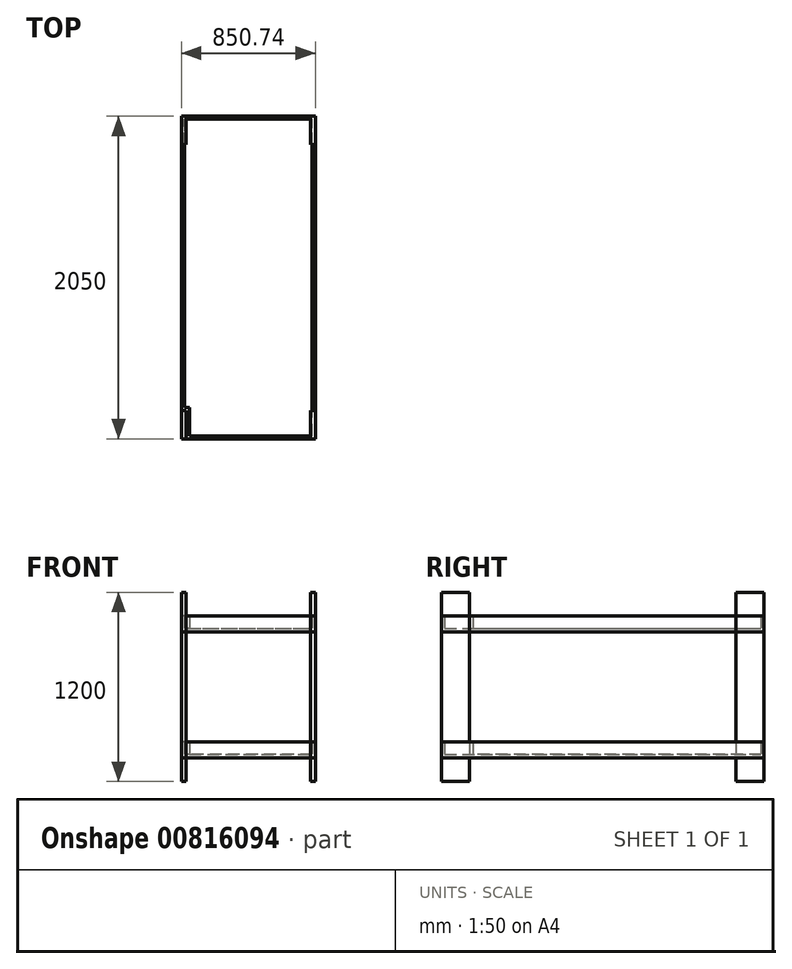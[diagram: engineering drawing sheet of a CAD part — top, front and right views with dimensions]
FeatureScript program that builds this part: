
annotation { "Feature Type Name" : "Feature", "Feature Type Description" : "" }
export const myFeature = defineFeature(function(context is Context, id is Id, definition is map)
    precondition{}
    {
        {
            var Q0;
            Q0=qCreatedBy(makeId("Top.planeOp"),FACE);
            var sketch = newSketch(context, id + "F0", { "sketchPlane" : qUnion([Q0])});
            skLineSegment(sketch, "E0.bottom", {"start": v(-156.82, -88.98) * mm, "end": v(-186.82, -88.98) * mm});
            skLineSegment(sketch, "E0.top", {"start": v(-156.82, 91.02) * mm, "end": v(-186.82, 91.02) * mm});
            skLineSegment(sketch, "E0.left", {"start": v(-156.82, -88.98) * mm, "end": v(-156.82, 91.02) * mm});
            skLineSegment(sketch, "E0.right", {"start": v(-186.82, -88.98) * mm, "end": v(-186.82, 91.02) * mm});
            skPoint(sketch, "E0.middle", {"position": v(-171.82, 1.02) * mm});
            skLineSegment(sketch, "E1.bottom", {"start": v(663.18, 1781.02) * mm, "end": v(633.18, 1781.02) * mm});
            skLineSegment(sketch, "E1.top", {"start": v(663.18, 1961.02) * mm, "end": v(633.18, 1961.02) * mm});
            skLineSegment(sketch, "E1.left", {"start": v(663.18, 1781.02) * mm, "end": v(663.18, 1961.02) * mm});
            skLineSegment(sketch, "E1.right", {"start": v(633.18, 1781.02) * mm, "end": v(633.18, 1961.02) * mm});
            skPoint(sketch, "E1.middle", {"position": v(648.18, 1871.02) * mm});
            skLineSegment(sketch, "E2.bottom", {"start": v(663.18, -88.98) * mm, "end": v(633.18, -88.98) * mm});
            skLineSegment(sketch, "E2.top", {"start": v(663.18, 91.02) * mm, "end": v(633.18, 91.02) * mm});
            skLineSegment(sketch, "E2.left", {"start": v(663.18, -88.98) * mm, "end": v(663.18, 91.02) * mm});
            skLineSegment(sketch, "E2.right", {"start": v(633.18, -88.98) * mm, "end": v(633.18, 91.02) * mm});
            skPoint(sketch, "E2.middle", {"position": v(648.18, 1.02) * mm});
            skLineSegment(sketch, "E3.bottom", {"start": v(-156.82, 1781.02) * mm, "end": v(-186.82, 1781.02) * mm});
            skLineSegment(sketch, "E3.top", {"start": v(-156.82, 1961.02) * mm, "end": v(-186.82, 1961.02) * mm});
            skLineSegment(sketch, "E3.left", {"start": v(-156.82, 1781.02) * mm, "end": v(-156.82, 1961.02) * mm});
            skLineSegment(sketch, "E3.right", {"start": v(-186.82, 1781.02) * mm, "end": v(-186.82, 1961.02) * mm});
            skPoint(sketch, "E3.middle", {"position": v(-171.82, 1871.02) * mm});
            skLineSegment(sketch, "E4", {"start": v(-186.82, -88.98) * mm, "end": v(663.18, -88.98) * mm, "construction": true});
            skLineSegment(sketch, "E5", {"start": v(-186.82, 1961.02) * mm, "end": v(663.18, 1961.02) * mm, "construction": true});
            skLineSegment(sketch, "E6", {"start": v(-186.82, 1961.02) * mm, "end": v(-186.82, -88.98) * mm, "construction": true});
            skLineSegment(sketch, "E7", {"start": v(663.18, 1961.02) * mm, "end": v(663.18, -88.98) * mm, "construction": true});
            skSolve(sketch);
        }
        {
            var Q0;
            Q0=makeQuery(id+"F0.imprint","IMPRINT",FACE,{"disambiguationData":[TD([[makeQuery(id+"F0.imprint","IMPRINT",EDGE,{"derivedFrom":sQuery(id+"F0.wireOp",EDGE,"E3.bottom")}),-1.0]])]});
            var Q1;
            Q1=makeQuery(id+"F0.imprint","IMPRINT",FACE,{"disambiguationData":[TD([[makeQuery(id+"F0.imprint","IMPRINT",EDGE,{"derivedFrom":sQuery(id+"F0.wireOp",EDGE,"E1.bottom")}),-1.0]])]});
            var Q2;
            Q2=makeQuery(id+"F0.imprint","IMPRINT",FACE,{"disambiguationData":[TD([[makeQuery(id+"F0.imprint","IMPRINT",EDGE,{"derivedFrom":sQuery(id+"F0.wireOp",EDGE,"E0.bottom")}),-1.0]])]});
            var Q3;
            Q3=makeQuery(id+"F0.imprint","IMPRINT",FACE,{"disambiguationData":[TD([[makeQuery(id+"F0.imprint","IMPRINT",EDGE,{"derivedFrom":sQuery(id+"F0.wireOp",EDGE,"E2.bottom")}),-1.0]])]});
            extrude(context, id + "F1", {"entities" : qUnion([Q0, Q1, Q2, Q3]), "depth" : 150 * mm, "offsetDistance" : 25 * mm});
        }
        {
            var Q0;
            Q0=makeQuery(id+"F1.opExtrude","CAP_FACE",FACE,{"disambiguationData":[OSD([sQuery(id+"F0.wireOp",EDGE,"E0.bottom"),sQuery(id+"F0.wireOp",EDGE,"E0.top"),sQuery(id+"F0.wireOp",EDGE,"E0.left"),sQuery(id+"F0.wireOp",EDGE,"E0.right")])],"isStart":false});
            var sketch = newSketch(context, id + "F2", { "sketchPlane" : qUnion([Q0])});
            skLineSegment(sketch, "E8", {"start": v(-186.82, -88.98) * mm, "end": v(663.92, -88.98) * mm});
            skLineSegment(sketch, "E9", {"start": v(663.92, -88.98) * mm, "end": v(663.18, 1961.02) * mm});
            skLineSegment(sketch, "E10", {"start": v(663.18, 1961.02) * mm, "end": v(-186.82, 1961.02) * mm});
            skLineSegment(sketch, "E11", {"start": v(-186.82, 1961.02) * mm, "end": v(-186.82, -88.98) * mm});
            skSolve(sketch);
        }
        {
            var Q0;
            {var subQ3=sQuery(id+"F2.wireOp",EDGE,"E9");Q0=makeQuery(id+"F2.imprint","IMPRINT",FACE,{"disambiguationData":[TD([[makeQuery(id+"F2.imprint","IMPRINT",EDGE,{"derivedFrom":subQ3}),1.0]])]});}
            extrude(context, id + "F3", {"entities" : qUnion([Q0]), "depth" : 100 * mm, "offsetDistance" : 25 * mm});
        }
        {
            var Q0;
            Q0=makeQuery(id+"F1.opExtrude","CAP_FACE",FACE,{"disambiguationData":[OSD([sQuery(id+"F0.wireOp",EDGE,"E1.bottom"),sQuery(id+"F0.wireOp",EDGE,"E1.top"),sQuery(id+"F0.wireOp",EDGE,"E1.left"),sQuery(id+"F0.wireOp",EDGE,"E1.right")])],"isStart":false});
            var Q1;
            Q1=makeQuery(id+"F1.opExtrude","CAP_FACE",FACE,{"disambiguationData":[OSD([sQuery(id+"F0.wireOp",EDGE,"E3.bottom"),sQuery(id+"F0.wireOp",EDGE,"E3.top"),sQuery(id+"F0.wireOp",EDGE,"E3.left"),sQuery(id+"F0.wireOp",EDGE,"E3.right")])],"isStart":false});
            var Q2;
            Q2=makeQuery(id+"F1.opExtrude","CAP_FACE",FACE,{"disambiguationData":[OSD([sQuery(id+"F0.wireOp",EDGE,"E2.bottom"),sQuery(id+"F0.wireOp",EDGE,"E2.top"),sQuery(id+"F0.wireOp",EDGE,"E2.left"),sQuery(id+"F0.wireOp",EDGE,"E2.right")])],"isStart":false});
            var Q3;
            Q3=makeQuery(id+"F1.opExtrude","CAP_FACE",FACE,{"disambiguationData":[OSD([sQuery(id+"F0.wireOp",EDGE,"E0.bottom"),sQuery(id+"F0.wireOp",EDGE,"E0.top"),sQuery(id+"F0.wireOp",EDGE,"E0.left"),sQuery(id+"F0.wireOp",EDGE,"E0.right")])],"isStart":false});
            extrude(context, id + "F4", {"entities" : qUnion([Q0, Q1, Q2, Q3]), "depth" : 800 * mm, "offsetDistance" : 25 * mm});
        }
        {
            var Q0;
            Q0=makeQuery(id+"F3.opExtrude","CAP_FACE",FACE,{"disambiguationData":[OSD([sQuery(id+"F0.wireOp",EDGE,"E0.top"),sQuery(id+"F0.wireOp",EDGE,"E0.left"),sQuery(id+"F2.wireOp",EDGE,"E8"),sQuery(id+"F2.wireOp",EDGE,"E9"),sQuery(id+"F2.wireOp",EDGE,"E10"),sQuery(id+"F2.wireOp",EDGE,"E11")])],"isStart":false});
            shell(context, id + "F5", {"entities" : qUnion([Q0]), "thickness" : 20 * mm});
        }
        {
            var Q0;
            Q0=makeQuery(id+"F4.opExtrude","CAP_FACE",FACE,{"disambiguationData":[OSD([sQuery(id+"F0.wireOp",EDGE,"E0.bottom"),sQuery(id+"F0.wireOp",EDGE,"E0.top"),sQuery(id+"F0.wireOp",EDGE,"E0.left"),sQuery(id+"F0.wireOp",EDGE,"E0.right")])],"isStart":false});
            var sketch = newSketch(context, id + "F6", { "sketchPlane" : qUnion([Q0])});
            skLineSegment(sketch, "E12", {"start": v(-186.82, -88.98) * mm, "end": v(663.18, -88.98) * mm});
            skLineSegment(sketch, "E13", {"start": v(-186.82, -88.98) * mm, "end": v(-186.82, 1961.02) * mm});
            skLineSegment(sketch, "E14", {"start": v(-186.82, 1961.02) * mm, "end": v(663.18, 1961.02) * mm});
            skLineSegment(sketch, "E15", {"start": v(663.18, -88.98) * mm, "end": v(663.18, 1961.02) * mm});
            skSolve(sketch);
        }
        {
            var Q0;
            Q0=makeQuery(id+"F4.opExtrude","CAP_FACE",FACE,{"disambiguationData":[OSD([sQuery(id+"F0.wireOp",EDGE,"E2.bottom"),sQuery(id+"F0.wireOp",EDGE,"E2.top"),sQuery(id+"F0.wireOp",EDGE,"E2.left"),sQuery(id+"F0.wireOp",EDGE,"E2.right")])],"isStart":false});
            var Q1;
            Q1=makeQuery(id+"F4.opExtrude","CAP_FACE",FACE,{"disambiguationData":[OSD([sQuery(id+"F0.wireOp",EDGE,"E0.bottom"),sQuery(id+"F0.wireOp",EDGE,"E0.top"),sQuery(id+"F0.wireOp",EDGE,"E0.left"),sQuery(id+"F0.wireOp",EDGE,"E0.right")])],"isStart":false});
            var Q2;
            Q2=makeQuery(id+"F4.opExtrude","CAP_FACE",FACE,{"disambiguationData":[OSD([sQuery(id+"F0.wireOp",EDGE,"E3.bottom"),sQuery(id+"F0.wireOp",EDGE,"E3.top"),sQuery(id+"F0.wireOp",EDGE,"E3.left"),sQuery(id+"F0.wireOp",EDGE,"E3.right")])],"isStart":false});
            var Q3;
            Q3=makeQuery(id+"F4.opExtrude","CAP_FACE",FACE,{"disambiguationData":[OSD([sQuery(id+"F0.wireOp",EDGE,"E1.bottom"),sQuery(id+"F0.wireOp",EDGE,"E1.top"),sQuery(id+"F0.wireOp",EDGE,"E1.left"),sQuery(id+"F0.wireOp",EDGE,"E1.right")])],"isStart":false});
            extrude(context, id + "F7", {"entities" : qUnion([Q0, Q1, Q2, Q3]), "depth" : 250 * mm, "offsetDistance" : 25 * mm});
        }
        {
            var Q0;
            {var subQ0=sQuery(id+"F6.wireOp",EDGE,"E14");Q0=makeQuery(id+"F6.imprint","IMPRINT",FACE,{"disambiguationData":[TD([[makeQuery(id+"F6.imprint","IMPRINT",EDGE,{"derivedFrom":subQ0}),-1.0]])]});}
            extrude(context, id + "F8", {"entities" : qUnion([Q0]), "depth" : 100 * mm, "offsetDistance" : 25 * mm});
        }
        {
            var Q0;
            Q0=makeQuery(id+"F8.opExtrude","CAP_FACE",FACE,{"disambiguationData":[OSD([sQuery(id+"F0.wireOp",EDGE,"E0.top"),sQuery(id+"F0.wireOp",EDGE,"E0.left"),sQuery(id+"F6.wireOp",EDGE,"E12"),sQuery(id+"F6.wireOp",EDGE,"E13"),sQuery(id+"F6.wireOp",EDGE,"E14"),sQuery(id+"F6.wireOp",EDGE,"E15")])],"isStart":false});
            shell(context, id + "F9", {"entities" : qUnion([Q0]), "thickness" : 20 * mm});
        }
    });
